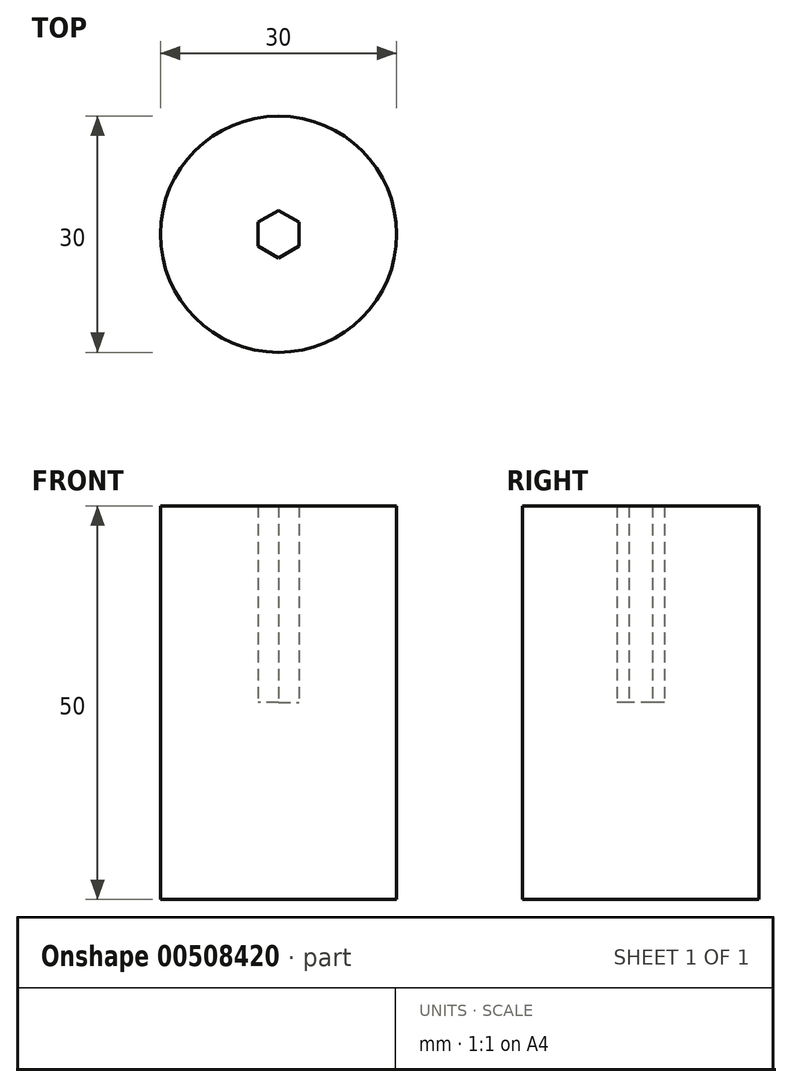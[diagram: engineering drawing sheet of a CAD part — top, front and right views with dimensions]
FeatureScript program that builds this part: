
annotation { "Feature Type Name" : "Feature", "Feature Type Description" : "" }
export const myFeature = defineFeature(function(context is Context, id is Id, definition is map)
    precondition{}
    {
        {
            var Q0;
            Q0=qCreatedBy(makeId("Top.planeOp"),FACE);
            var sketch = newSketch(context, id + "F0", { "sketchPlane" : qUnion([Q0])});
            skCircle(sketch, "E0", {"center": v(0, 0) * mm, "radius": 15 * mm});
            skCircle(sketch, "E1.cCircle", {"center": v(0, 0) * mm, "radius": 2.62 * mm, "construction": true});
            skLineSegment(sketch, "E1.0", {"start": v(2.62, 1.52) * mm, "end": v(2.62, -1.52) * mm});
            skLineSegment(sketch, "E1.1", {"start": v(2.63, -1.52) * mm, "end": v(0, -3.03) * mm});
            skLineSegment(sketch, "E1.2", {"start": v(0, -3.03) * mm, "end": v(-2.63, -1.52) * mm});
            skLineSegment(sketch, "E1.3", {"start": v(-2.62, -1.52) * mm, "end": v(-2.63, 1.52) * mm});
            skLineSegment(sketch, "E1.4", {"start": v(-2.63, 1.52) * mm, "end": v(0, 3.03) * mm});
            skLineSegment(sketch, "E1.5", {"start": v(0, 3.03) * mm, "end": v(2.63, 1.52) * mm});
            skPoint(sketch, "E1.0.midPoint", {"position": v(2.62, 0) * mm});
            skSolve(sketch);
        }
        {
            var Q0;
            Q0=makeQuery(id+"F0.imprint","IMPRINT",FACE,{"disambiguationData":[TD([[makeQuery(id+"F0.imprint","IMPRINT",EDGE,{"derivedFrom":sQuery(id+"F0.wireOp",EDGE,"E0")}),1.0]])]});
            extrude(context, id + "F1", {"entities" : qUnion([Q0]), "depth" : 50 * mm});
        }
        {
            var Q0;
            Q0=makeQuery(id+"F0.imprint","IMPRINT",FACE,{"disambiguationData":[TD([[makeQuery(id+"F0.imprint","IMPRINT",EDGE,{"derivedFrom":sQuery(id+"F0.wireOp",EDGE,"E1.0")}),-1.0]])]});
            extrude(context, id + "F2", {"entities" : qUnion([Q0]), "operationType" : NewBodyOperationType.ADD, "depth" : 25 * mm});
        }
    });
